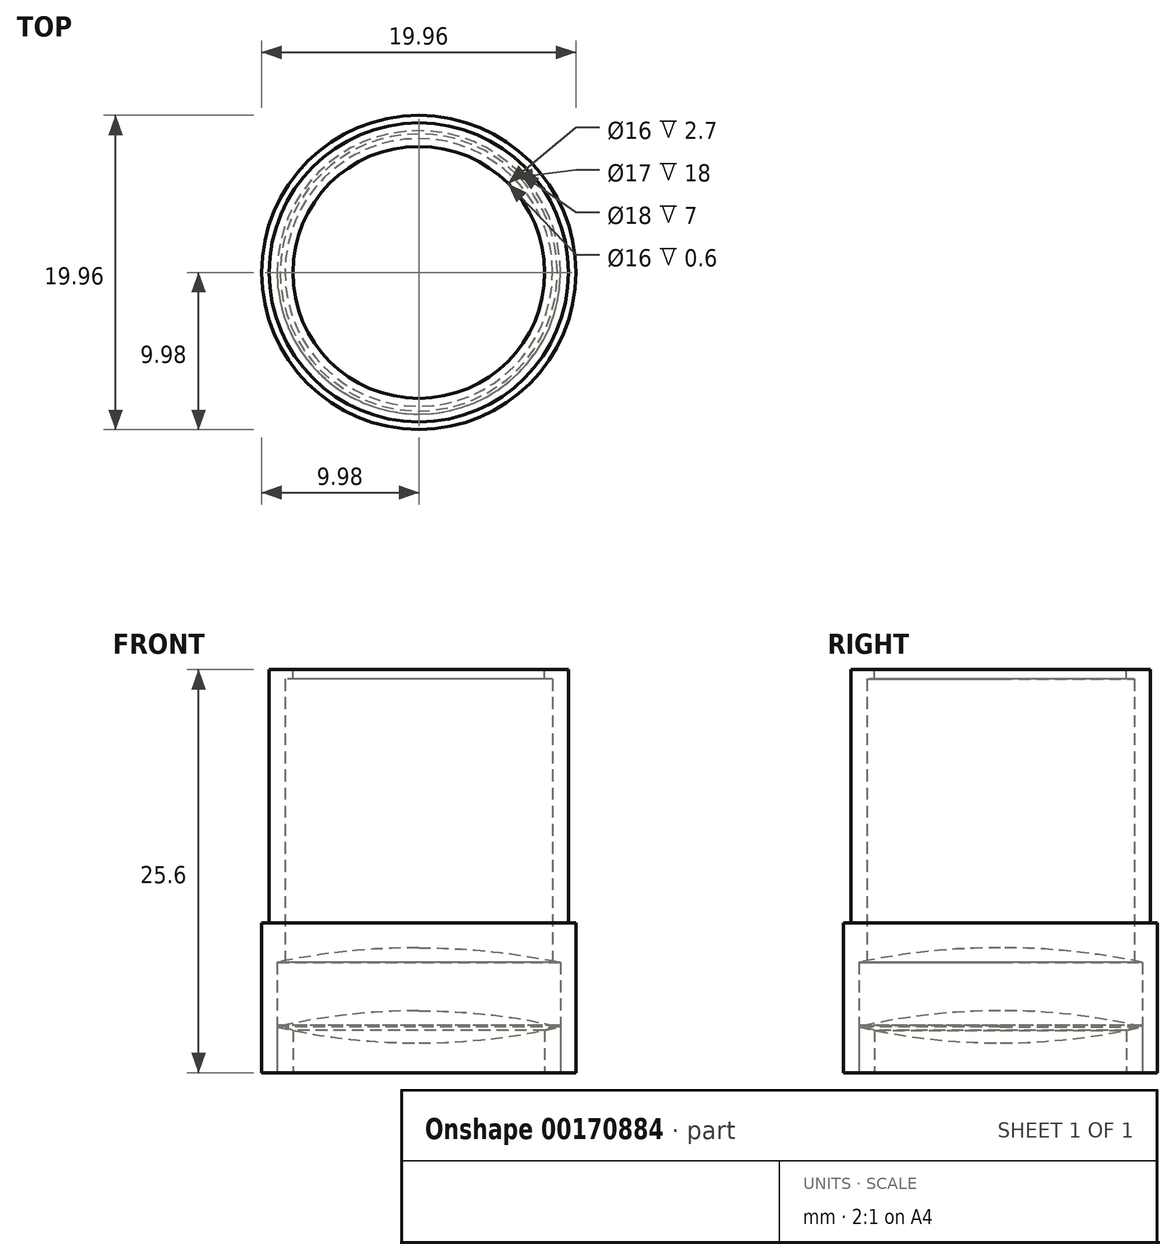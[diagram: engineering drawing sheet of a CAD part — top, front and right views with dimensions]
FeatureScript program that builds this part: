
annotation { "Feature Type Name" : "Feature", "Feature Type Description" : "" }
export const myFeature = defineFeature(function(context is Context, id is Id, definition is map)
    precondition{}
    {
        {
            var Q0;
            Q0=qCreatedBy(makeId("Top.planeOp"),FACE);
            var sketch = newSketch(context, id + "F0", { "sketchPlane" : qUnion([Q0])});
            skCircle(sketch, "E0", {"center": v(0, 0) * mm, "radius": 8.5 * mm});
            skCircle(sketch, "E1", {"center": v(0, 0) * mm, "radius": 9.5 * mm});
            skCircle(sketch, "E2", {"center": v(0, 0) * mm, "radius": 9.97 * mm});
            skCircle(sketch, "E3", {"center": v(0, 0) * mm, "radius": 8 * mm});
            skCircle(sketch, "E4", {"center": v(0, 0) * mm, "radius": 9 * mm});
            skCircle(sketch, "E5", {"center": v(0, 0) * mm, "radius": 8.4 * mm});
            skSolve(sketch);
        }
        {
            var Q0;
            Q0=makeQuery(id+"F0.imprint","IMPRINT",FACE,{"disambiguationData":[TD([[makeQuery(id+"F0.imprint","IMPRINT",EDGE,{"derivedFrom":sQuery(id+"F0.wireOp",EDGE,"E1")}),1.0]])]});
            var Q1;
            Q1=makeQuery(id+"F0.imprint","IMPRINT",FACE,{"disambiguationData":[TD([[makeQuery(id+"F0.imprint","IMPRINT",EDGE,{"derivedFrom":sQuery(id+"F0.wireOp",EDGE,"E1")}),-1.0]])]});
            extrude(context, id + "F1", {"entities" : qUnion([Q0, Q1]), "depth" : 9.5 * mm});
        }
        {
            var Q0;
            Q0=makeQuery(id+"F1.opExtrude","CAP_FACE",FACE,{"disambiguationData":[OSD([sQuery(id+"F0.wireOp",EDGE,"E2"),sQuery(id+"F0.wireOp",EDGE,"E4")])],"isStart":false});
            cPlane(context, id + "F2", {"entities" : qUnion([Q0]), "cplaneType" : CPlaneType.OFFSET, "offset" : 2.5 * mm, "oppositeDirection" : true, "width" : 150 * mm, "height" : 150 * mm});
        }
        {
            var Q0;
            Q0=qCreatedBy(id+"F2.planeOp",FACE);
            var sketch = newSketch(context, id + "F3", { "sketchPlane" : qUnion([Q0])});
            skCircle(sketch, "E6.0", {"center": v(0, 0) * mm, "radius": 9.5 * mm});
            skCircle(sketch, "E7.0", {"center": v(0, 0) * mm, "radius": 8.5 * mm});
            skSolve(sketch);
        }
        {
            var Q0;
            Q0=makeQuery(id+"F3.imprint","IMPRINT",FACE,{"disambiguationData":[TD([[makeQuery(id+"F3.imprint","IMPRINT",EDGE,{"derivedFrom":sQuery(id+"F3.wireOp",EDGE,"E6.0")}),1.0]])]});
            extrude(context, id + "F4", {"entities" : qUnion([Q0]), "operationType" : NewBodyOperationType.ADD, "depth" : 18.6 * mm});
        }
        {
            var Q0;
            Q0=makeQuery(id+"F4.opExtrude","CAP_FACE",FACE,{"disambiguationData":[OSD([sQuery(id+"F3.wireOp",EDGE,"E6.0"),sQuery(id+"F3.wireOp",EDGE,"E7.0")])],"isStart":false});
            cPlane(context, id + "F5", {"entities" : qUnion([Q0]), "cplaneType" : CPlaneType.OFFSET, "offset" : 0 * mm, "width" : 150 * mm, "height" : 150 * mm});
        }
        {
            var Q0;
            Q0=qCreatedBy(id+"F5.planeOp",FACE);
            var sketch = newSketch(context, id + "F6", { "sketchPlane" : qUnion([Q0])});
            skCircle(sketch, "E8.0", {"center": v(0, 0) * mm, "radius": 8 * mm});
            skCircle(sketch, "E9.0", {"center": v(0, 0) * mm, "radius": 8.5 * mm});
            skSolve(sketch);
        }
        {
            var Q0;
            Q0=makeQuery(id+"F6.imprint","IMPRINT",FACE,{"disambiguationData":[TD([[makeQuery(id+"F6.imprint","IMPRINT",EDGE,{"derivedFrom":sQuery(id+"F6.wireOp",EDGE,"E8.0")}),-1.0]])]});
            extrude(context, id + "F7", {"entities" : qUnion([Q0]), "operationType" : NewBodyOperationType.ADD, "oppositeDirection" : true, "depth" : 0.6 * mm});
        }
        {
            var Q0;
            Q0=makeQuery(id+"F0.imprint","IMPRINT",FACE,{"disambiguationData":[TD([[makeQuery(id+"F0.imprint","IMPRINT",EDGE,{"derivedFrom":sQuery(id+"F0.wireOp",EDGE,"E3")}),-1.0]])]});
            var Q1;
            Q1=makeQuery(id+"F0.imprint","IMPRINT",FACE,{"disambiguationData":[TD([[makeQuery(id+"F0.imprint","IMPRINT",EDGE,{"derivedFrom":sQuery(id+"F0.wireOp",EDGE,"E0")}),1.0]])]});
            var Q2;
            Q2=makeQuery(id+"F0.imprint","IMPRINT",FACE,{"disambiguationData":[TD([[makeQuery(id+"F0.imprint","IMPRINT",EDGE,{"derivedFrom":sQuery(id+"F0.wireOp",EDGE,"E0")}),-1.0]])]});
            extrude(context, id + "F8", {"entities" : qUnion([Q0, Q1, Q2]), "depth" : 3 * mm});
        }
        {
            var Q0;
            Q0=makeQuery(id+"F8.opExtrude","CAP_EDGE",EDGE,{"disambiguationData":[OSD([sQuery(id+"F0.wireOp",EDGE,"E3")])],"isStart":false});
            chamfer(context, id + "F9", {"entities" : qUnion([Q0]), "chamferType" : ChamferType.TWO_OFFSETS, "width1" : .3 * mm, "oppositeDirection" : false, "width2" : .8 * mm, "tangentPropagation" : true});
        }
        {
            var Q0;
            Q0=qCreatedBy(makeId("Front.planeOp"),FACE);
            var sketch = newSketch(context, id + "F10", { "sketchPlane" : qUnion([Q0])});
            skLineSegment(sketch, "E10", {"start": v(0, -11.14) * mm, "end": v(0, 30.62) * mm, "construction": true});
            skLineSegment(sketch, "E11", {"start": v(-15.85, 0) * mm, "end": v(14.87, 0) * mm, "construction": true});
            skArc(sketch, "E12", {"start": v(9, 2.91) * mm, "mid": v(4.53, 3.68) * mm, "end": v(0, 3.94) * mm});
            skArc(sketch, "E13.0", {"start": v(9, 7) * mm, "mid": v(4.52, 7.7) * mm, "end": v(0, 7.94) * mm});
            skLineSegment(sketch, "E14", {"start": v(0, 7.94) * mm, "end": v(0, 3.94) * mm});
            skArc(sketch, "E15.MirrorCS", {"start": v(9, 2.91) * mm, "mid": v(4.53, 2.14) * mm, "end": v(0, 1.89) * mm});
            skLineSegment(sketch, "E16", {"start": v(0, 3.94) * mm, "end": v(0, 1.89) * mm});
            skLineSegment(sketch, "E17", {"start": v(9, 7) * mm, "end": v(9, 2.91) * mm});
            skSolve(sketch);
        }
        {
            var Q0;
            {var subQ0=sQuery(id+"F10.wireOp",EDGE,"E12");Q0=makeQuery(id+"F10.imprint","IMPRINT",FACE,{"disambiguationData":[TD([[makeQuery(id+"F10.imprint","IMPRINT",EDGE,{"derivedFrom":subQ0}),-1.0]])]});}
            var Q1;
            Q1=sQuery(id+"F10.wireOp",EDGE,"E10");
            revolve(context, id + "F11", {"entities" : qUnion([Q0]), "axis" : qUnion([Q1]), "revolveType" : RevolveType.FULL});
        }
        {
            var Q0;
            {var subQ4=sQuery(id+"F10.wireOp",EDGE,"E12");Q0=makeQuery(id+"F10.imprint","IMPRINT",FACE,{"disambiguationData":[TD([[makeQuery(id+"F10.imprint","IMPRINT",EDGE,{"derivedFrom":subQ4}),1.0]])]});}
            var Q1;
            {var subQ0=sQuery(id+"F10.wireOp",EDGE,"E15.MirrorCS");Q1=makeQuery(id+"F10.imprint","IMPRINT",FACE,{"disambiguationData":[TD([[makeQuery(id+"F10.imprint","IMPRINT",EDGE,{"derivedFrom":subQ0}),-1.0]])]});}
            var Q2;
            Q2=sQuery(id+"F10.wireOp",EDGE,"E10");
            revolve(context, id + "F12", {"entities" : qUnion([Q0, Q1]), "axis" : qUnion([Q2]), "revolveType" : RevolveType.FULL});
        }
    });
